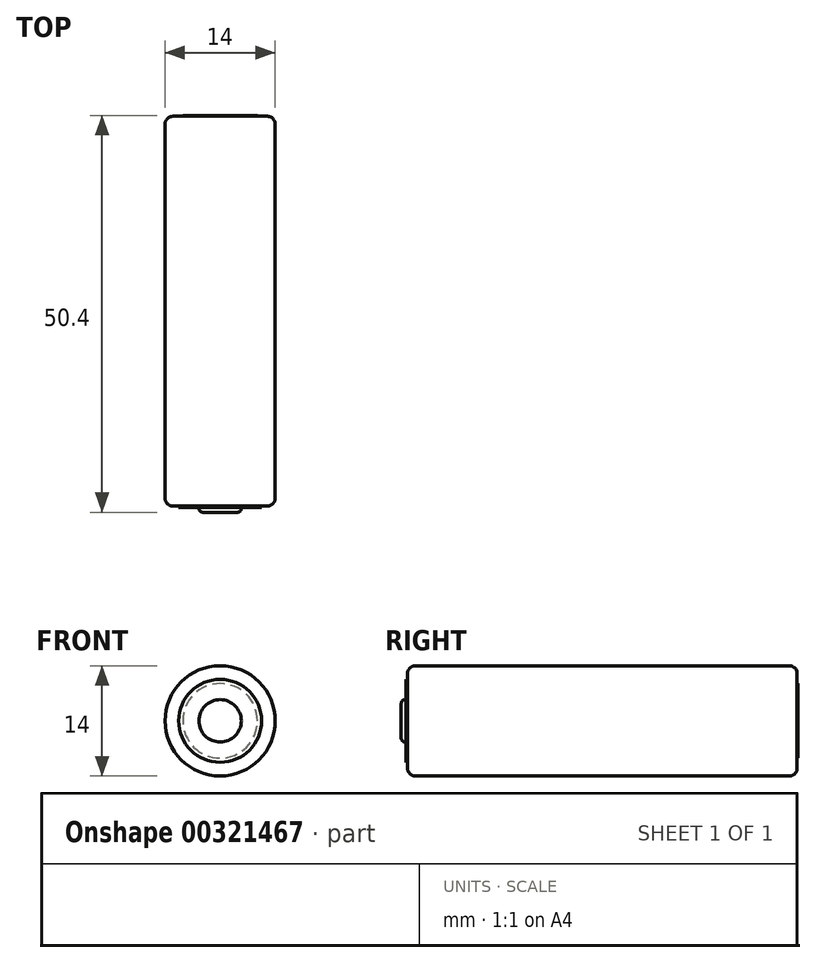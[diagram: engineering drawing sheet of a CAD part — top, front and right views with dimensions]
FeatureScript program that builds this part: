
annotation { "Feature Type Name" : "Feature", "Feature Type Description" : "" }
export const myFeature = defineFeature(function(context is Context, id is Id, definition is map)
    precondition{}
    {
        {
            var Q0;
            Q0=qCreatedBy(makeId("Front.planeOp"),FACE);
            var sketch = newSketch(context, id + "F0", { "sketchPlane" : qUnion([Q0])});
            skCircle(sketch, "E0", {"center": v(0, 0) * mm, "radius": 7 * mm});
            skSolve(sketch);
        }
        {
            var Q0;
            Q0 = qSketchRegion(id + "F0", true);
            extrude(context, id + "F1", {"entities" : qUnion([Q0]), "depth" : 49.5 * mm});
        }
        {
            var Q0;
            Q0=makeQuery(id+"F1.opExtrude","CAP_FACE",FACE,{"disambiguationData":[OSD([sQuery(id+"F0.wireOp",EDGE,"E0")])],"isStart":false});
            var sketch = newSketch(context, id + "F2", { "sketchPlane" : qUnion([Q0])});
            skCircle(sketch, "E1", {"center": v(0, 0) * mm, "radius": 5.27 * mm});
            skSolve(sketch);
        }
        {
            var Q0;
            Q0 = qSketchRegion(id + "F2", true);
            extrude(context, id + "F3", {"entities" : qUnion([Q0]), "depth" : .2 * mm});
        }
        {
            var Q0;
            Q0=makeQuery(id+"F1.opExtrude","CAP_EDGE",EDGE,{"disambiguationData":[OSD([sQuery(id+"F0.wireOp",EDGE,"E0")])],"isStart":false});
            var Q1;
            Q1=makeQuery(id+"F1.opExtrude","CAP_EDGE",EDGE,{"disambiguationData":[OSD([sQuery(id+"F0.wireOp",EDGE,"E0")])],"isStart":true});
            fillet(context, id + "F4", {"entities" : qUnion([Q0, Q1]), "radius" : 1 * mm, "tangentPropagation" : true, "allowEdgeOverflow" : false});
        }
        {
            var Q0;
            Q0=makeQuery(id+"F3.opExtrude","CAP_FACE",FACE,{"disambiguationData":[OSD([sQuery(id+"F2.wireOp",EDGE,"E1")])],"isStart":false});
            var sketch = newSketch(context, id + "F5", { "sketchPlane" : qUnion([Q0])});
            skCircle(sketch, "E2", {"center": v(0, 0) * mm, "radius": 2.7 * mm});
            skSolve(sketch);
        }
        {
            var Q0;
            Q0 = qSketchRegion(id + "F5", true);
            extrude(context, id + "F6", {"entities" : qUnion([Q0]), "operationType" : NewBodyOperationType.ADD, "depth" : .6 * mm});
        }
        {
            var Q0;
            Q0=makeQuery(id+"F6.opExtrude","CAP_EDGE",EDGE,{"disambiguationData":[OSD([sQuery(id+"F5.wireOp",EDGE,"E2")])],"isStart":false});
            fillet(context, id + "F7", {"entities" : qUnion([Q0]), "radius" : .5 * mm, "tangentPropagation" : true, "allowEdgeOverflow" : false});
        }
        {
            var Q0;
            Q0=makeQuery(id+"F1.opExtrude","CAP_FACE",FACE,{"disambiguationData":[OSD([sQuery(id+"F0.wireOp",EDGE,"E0")])],"isStart":true});
            var sketch = newSketch(context, id + "F8", { "sketchPlane" : qUnion([Q0])});
            skCircle(sketch, "E3", {"center": v(0, 0) * mm, "radius": 4.73 * mm});
            skSolve(sketch);
        }
        {
            var Q0;
            Q0 = qSketchRegion(id + "F8", true);
            extrude(context, id + "F9", {"entities" : qUnion([Q0]), "depth" : .1 * mm});
        }
    });
